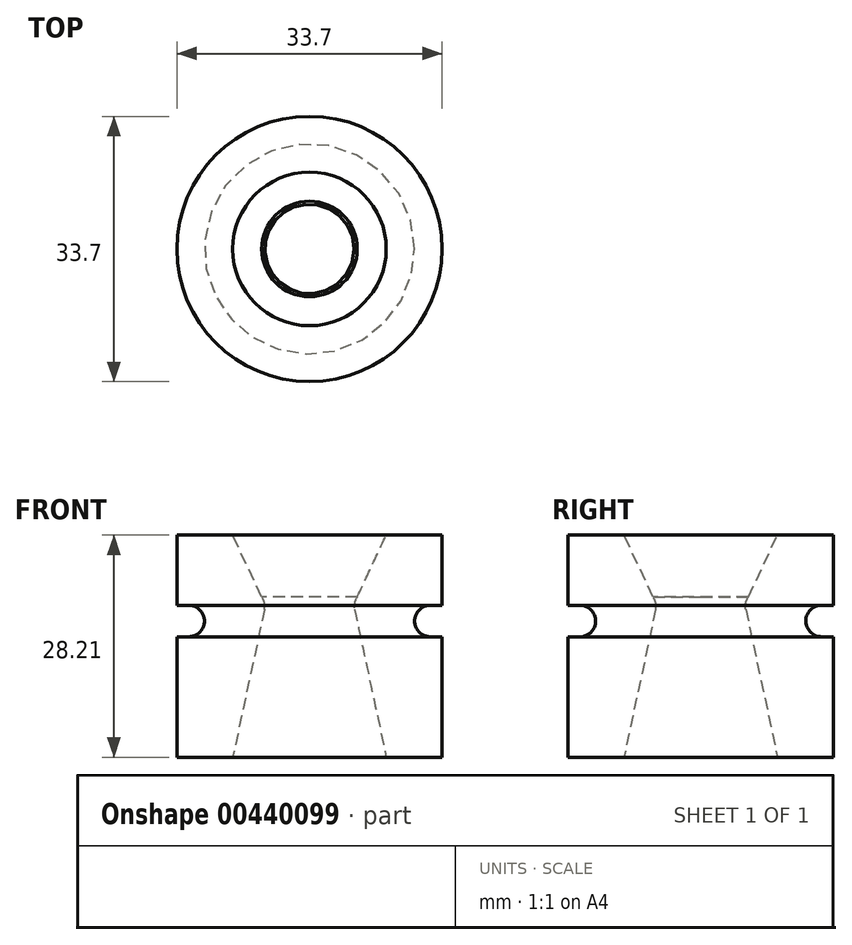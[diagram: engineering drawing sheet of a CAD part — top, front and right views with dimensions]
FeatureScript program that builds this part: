
annotation { "Feature Type Name" : "Feature", "Feature Type Description" : "" }
export const myFeature = defineFeature(function(context is Context, id is Id, definition is map)
    precondition{}
    {
        {
            var Q0;
            Q0=qCreatedBy(makeId("Top.planeOp"),FACE);
            var sketch = newSketch(context, id + "F0", { "sketchPlane" : qUnion([Q0])});
            skCircle(sketch, "E0", {"center": v(0, 0) * mm, "radius": 16.84 * mm});
            skCircle(sketch, "E1", {"center": v(0, 0) * mm, "radius": 9.75 * mm});
            skCircle(sketch, "E2", {"center": v(0, 0) * mm, "radius": 4.83 * mm});
            skSolve(sketch);
        }
        {
            var Q0;
            Q0=makeQuery(id+"F0.imprint","IMPRINT",FACE,{"disambiguationData":[TD([[makeQuery(id+"F0.imprint","IMPRINT",EDGE,{"derivedFrom":sQuery(id+"F0.wireOp",EDGE,"E0")}),1.0]])]});
            extrude(context, id + "F1", {"entities" : qUnion([Q0]), "depth" : 28.21 * mm, "offsetDistance" : 25 * mm});
        }
        {
            var Q0;
            Q0=makeQuery(id+"F0.imprint","IMPRINT",FACE,{"disambiguationData":[TD([[makeQuery(id+"F0.imprint","IMPRINT",EDGE,{"derivedFrom":sQuery(id+"F0.wireOp",EDGE,"E1")}),1.0]])]});
            extrude(context, id + "F2", {"entities" : qUnion([Q0]), "operationType" : NewBodyOperationType.ADD, "depth" : 28.21 * mm, "offsetDistance" : 25 * mm});
        }
        {
            var Q0;
            Q0=qCreatedBy(makeId("Front.planeOp"),FACE);
            var sketch = newSketch(context, id + "F3", { "sketchPlane" : qUnion([Q0])});
            skLineSegment(sketch, "E3", {"start": v(0, 0) * mm, "end": v(0, 28.2) * mm, "construction": true});
            skLineSegment(sketch, "E4", {"start": v(-16.84, 0) * mm, "end": v(16.84, 0) * mm});
            skLineSegment(sketch, "E5", {"start": v(16.84, 0) * mm, "end": v(16.84, 15.3) * mm, "construction": true});
            skLineSegment(sketch, "E6", {"start": v(16.84, 15.3) * mm, "end": v(16.84, 19.3) * mm});
            skLineSegment(sketch, "E7", {"start": v(16.84, 19.3) * mm, "end": v(16.84, 28.21) * mm, "construction": true});
            skLineSegment(sketch, "E8", {"start": v(16.84, 19.3) * mm, "end": v(15.34, 19.3) * mm});
            skLineSegment(sketch, "E9", {"start": v(15.34, 15.3) * mm, "end": v(16.84, 15.3) * mm});
            skArc(sketch, "E10", {"start": v(15.34, 19.3) * mm, "mid": v(13.34, 17.3) * mm, "end": v(15.34, 15.3) * mm});
            skPoint(sketch, "E11.orphan", {"position": v(13.84, 19.3) * mm});
            skPoint(sketch, "E12.orphan", {"position": v(13.84, 15.3) * mm});
            skLineSegment(sketch, "E13", {"start": v(15.34, 19.3) * mm, "end": v(15.34, 15.3) * mm, "construction": true});
            skLineSegment(sketch, "E14", {"start": v(16.84, 19.3) * mm, "end": v(0, 19.3) * mm, "construction": true});
            skLineSegment(sketch, "E15", {"start": v(0, 28.21) * mm, "end": v(9.75, 28.21) * mm});
            skLineSegment(sketch, "E16", {"start": v(9.75, 27.94) * mm, "end": v(9.75, 0) * mm, "construction": true});
            skLineSegment(sketch, "E17", {"start": v(5.72, 18.77) * mm, "end": v(9.75, 0) * mm});
            skPoint(sketch, "E18.visualSharp", {"position": v(5.6, 19.3) * mm});
            skArc(sketch, "E18.filletArc", {"start": v(6.07, 20.38) * mm, "mid": v(5.72, 19.62) * mm, "end": v(5.72, 18.77) * mm});
            skLineSegment(sketch, "E19", {"start": v(16.84, 0) * mm, "end": v(9.85, 0) * mm});
            skLineSegment(sketch, "E20", {"start": v(9.85, 0) * mm, "end": v(9.85, 28.21) * mm, "construction": true});
            skLineSegment(sketch, "E21", {"start": v(6.07, 20.38) * mm, "end": v(9.85, 28.21) * mm});
            skLineSegment(sketch, "E22", {"start": v(0, 0) * mm, "end": v(4.83, 0) * mm});
            skLineSegment(sketch, "E23", {"start": v(4.83, 0) * mm, "end": v(4.83, 28.21) * mm});
            skSolve(sketch);
        }
        {
            var Q0;
            Q0 = qSketchRegion(id + "F3", true);
            var Q1;
            Q1=sQuery(id+"F3.wireOp",EDGE,"E3");
            revolve(context, id + "F4", {"operationType" : NewBodyOperationType.REMOVE, "entities" : qUnion([Q0]), "axis" : qUnion([Q1]), "revolveType" : RevolveType.FULL, "oppositeDirection" : true});
        }
        {
            var Q0;
            Q0=qCreatedBy(makeId("Front.planeOp"),FACE);
            var sketch = newSketch(context, id + "F5", { "sketchPlane" : qUnion([Q0])});
            skArc(sketch, "E24.2", {"start": v(6.07, 20.38) * mm, "mid": v(5.72, 19.62) * mm, "end": v(5.72, 18.77) * mm});
            skLineSegment(sketch, "E24.3", {"start": v(5.72, 18.77) * mm, "end": v(9.75, 0) * mm});
            skLineSegment(sketch, "E24.4", {"start": v(0, 28.21) * mm, "end": v(9.75, 28.21) * mm});
            skLineSegment(sketch, "E24.5", {"start": v(0, 0) * mm, "end": v(0, 28.2) * mm});
            skLineSegment(sketch, "E24.6", {"start": v(9.75, 27.94) * mm, "end": v(9.75, 0) * mm, "construction": true});
            skLineSegment(sketch, "E24.7", {"start": v(16.84, 19.3) * mm, "end": v(0, 19.3) * mm});
            skLineSegment(sketch, "E24.8", {"start": v(-16.84, 0) * mm, "end": v(16.84, 0) * mm});
            skLineSegment(sketch, "E25", {"start": v(6.07, 20.38) * mm, "end": v(9.75, 28.21) * mm});
            skSolve(sketch);
        }
        {
            var Q0;
            Q0 = qSketchRegion(id + "F5", true);
            var Q1;
            Q1=sQuery(id+"F5.wireOp",EDGE,"E24.5");
            revolve(context, id + "F6", {"operationType" : NewBodyOperationType.REMOVE, "entities" : qUnion([Q0]), "axis" : qUnion([Q1]), "revolveType" : RevolveType.FULL, "oppositeDirection" : true});
        }
    });
